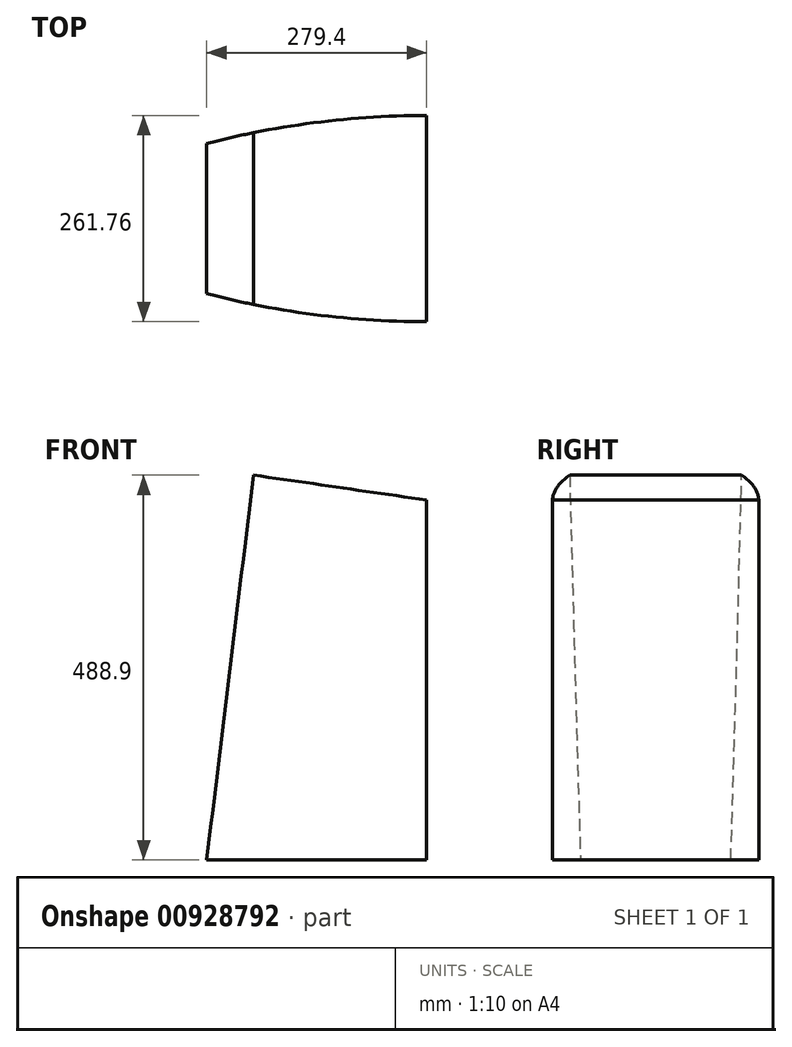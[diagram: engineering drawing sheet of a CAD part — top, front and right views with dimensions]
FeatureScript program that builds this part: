
annotation { "Feature Type Name" : "Feature", "Feature Type Description" : "" }
export const myFeature = defineFeature(function(context is Context, id is Id, definition is map)
    precondition{}
    {
        {
            var Q0;
            Q0=qCreatedBy(makeId("Front.planeOp"),FACE);
            var sketch = newSketch(context, id + "F0", { "sketchPlane" : qUnion([Q0])});
            skLineSegment(sketch, "E0", {"start": v(0, 0) * mm, "end": v(0, 457.2) * mm});
            skLineSegment(sketch, "E1", {"start": v(0, 457.2) * mm, "end": v(-219.97, 488.9) * mm});
            skLineSegment(sketch, "E2", {"start": v(-219.97, 488.9) * mm, "end": v(-279.4, 0) * mm});
            skLineSegment(sketch, "E3", {"start": v(-279.4, 0) * mm, "end": v(0, 0) * mm});
            skSolve(sketch);
        }
        {
            var Q0;
            Q0 = qSketchRegion(id + "F0", true);
            extrude(context, id + "F1", {"entities" : qUnion([Q0]), "endBound" : BoundingType.SYMMETRIC, "depth" : 304.8 * mm, "offsetDistance" : 25.4 * mm});
        }
        {
            var Q0;
            Q0=qCreatedBy(makeId("Top.planeOp"),FACE);
            var sketch = newSketch(context, id + "F2", { "sketchPlane" : qUnion([Q0])});
            skLineSegment(sketch, "E4", {"start": v(0, 0) * mm, "end": v(-279.4, 0) * mm, "construction": true});
            skArc(sketch, "E5", {"start": v(-279.4, -95.43) * mm, "mid": v(-140.84, -122.13) * mm, "end": v(0, -130.88) * mm});
            skLineSegment(sketch, "E6", {"start": v(0, -130.88) * mm, "end": v(-279.4, -131.46) * mm, "construction": true});
            skArc(sketch, "E7.MirrorCS", {"start": v(-279.4, 95.43) * mm, "mid": v(-140.84, 122.13) * mm, "end": v(0, 130.88) * mm});
            skLineSegment(sketch, "E8.MirrorCS", {"start": v(0, 130.88) * mm, "end": v(-279.4, 131.46) * mm, "construction": true});
            skLineSegment(sketch, "E9", {"start": v(-279.4, -95.43) * mm, "end": v(-279.4, -152.4) * mm});
            skLineSegment(sketch, "E10", {"start": v(-279.4, -152.4) * mm, "end": v(0, -152.4) * mm});
            skLineSegment(sketch, "E11", {"start": v(0, -152.4) * mm, "end": v(0, -130.88) * mm});
            skLineSegment(sketch, "E12", {"start": v(0, 130.88) * mm, "end": v(0, 152.4) * mm});
            skLineSegment(sketch, "E13", {"start": v(0, 152.4) * mm, "end": v(-279.4, 152.4) * mm});
            skLineSegment(sketch, "E14", {"start": v(-279.4, 152.4) * mm, "end": v(-279.4, 95.43) * mm});
            skSolve(sketch);
        }
        {
            var Q0;
            Q0 = qSketchRegion(id + "F2", true);
            extrude(context, id + "F3", {"entities" : qUnion([Q0]), "operationType" : NewBodyOperationType.REMOVE, "endBound" : BoundingType.THROUGH_ALL, "depth" : 25.4 * mm, "offsetDistance" : 25.4 * mm});
        }
    });
